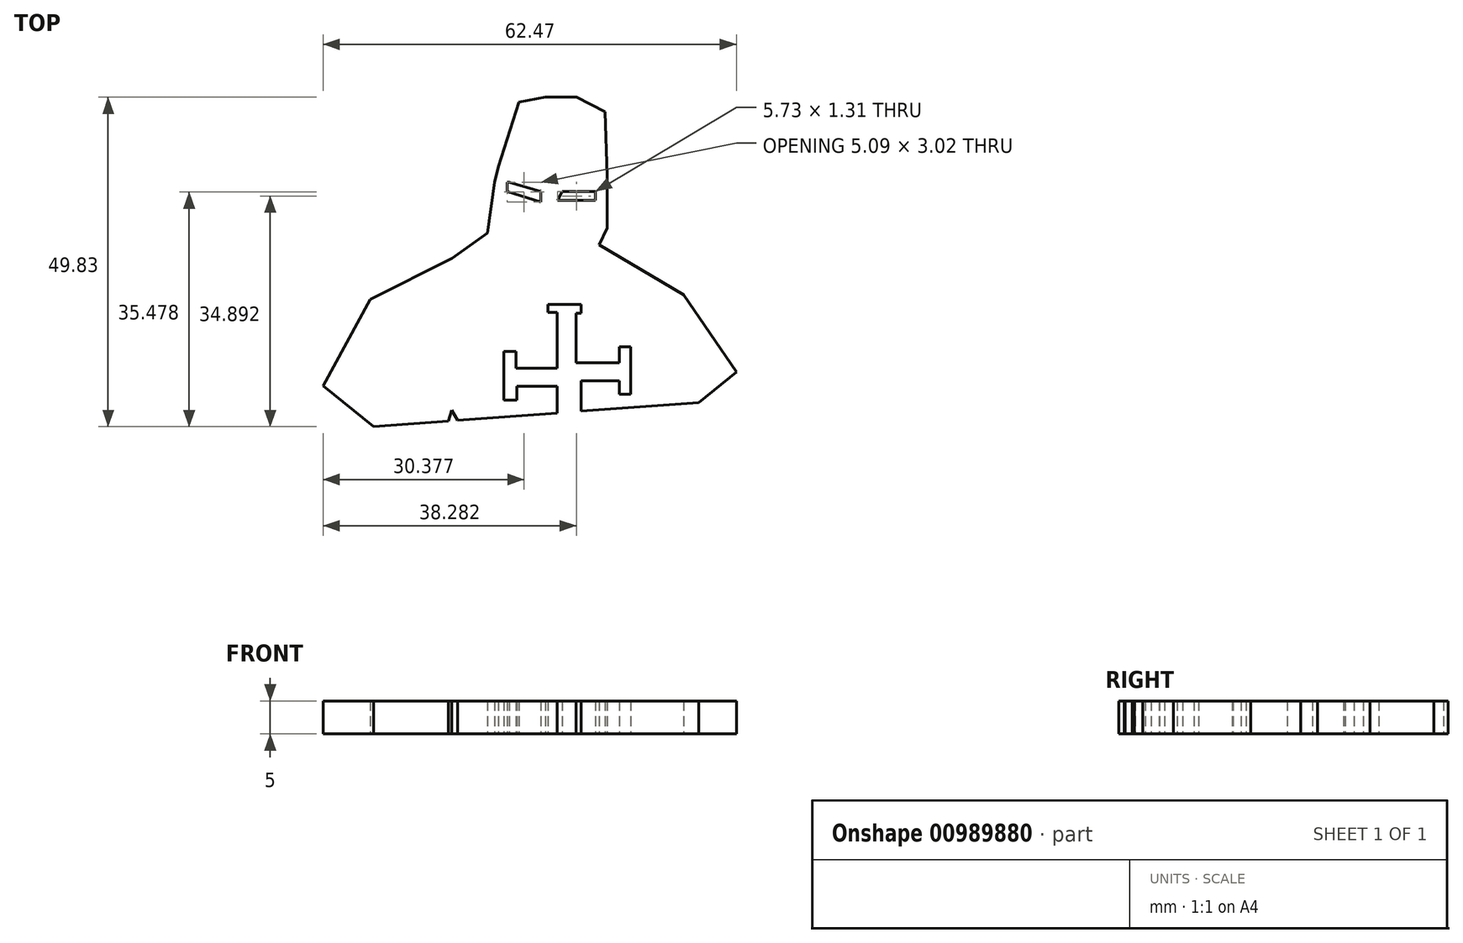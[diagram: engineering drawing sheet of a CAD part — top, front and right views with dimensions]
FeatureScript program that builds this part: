
annotation { "Feature Type Name" : "Feature", "Feature Type Description" : "" }
export const myFeature = defineFeature(function(context is Context, id is Id, definition is map)
    precondition{}
    {
        {
            var Q0;
            Q0=qCreatedBy(makeId("Top.planeOp"),FACE);
            var sketch = newSketch(context, id + "F0", { "sketchPlane" : qUnion([Q0])});
            skLineSegment(sketch, "E0", {"start": v(-38.63, 22.84) * mm, "end": v(-46.28, 28.98) * mm});
            skLineSegment(sketch, "E1", {"start": v(-46.28, 28.98) * mm, "end": v(-39.16, 42.1) * mm});
            skLineSegment(sketch, "E2", {"start": v(-39.16, 42.1) * mm, "end": v(-26.8, 48.3) * mm});
            skLineSegment(sketch, "E3", {"start": v(-26.8, 48.3) * mm, "end": v(-21.43, 52.1) * mm});
            skLineSegment(sketch, "E4", {"start": v(-21.43, 52.1) * mm, "end": v(-20.37, 59.83) * mm});
            skLineSegment(sketch, "E5", {"start": v(-20.37, 59.83) * mm, "end": v(-19.79, 62.17) * mm});
            skLineSegment(sketch, "E6", {"start": v(-19.79, 62.17) * mm, "end": v(-16.68, 71.92) * mm});
            skLineSegment(sketch, "E7", {"start": v(-16.68, 71.92) * mm, "end": v(-12.68, 72.67) * mm});
            skLineSegment(sketch, "E8", {"start": v(-12.68, 72.67) * mm, "end": v(-8, 72.67) * mm});
            skLineSegment(sketch, "E9", {"start": v(-8, 72.67) * mm, "end": v(-3.67, 70.46) * mm});
            skLineSegment(sketch, "E10", {"start": v(-3.67, 70.46) * mm, "end": v(-3.35, 60.81) * mm});
            skLineSegment(sketch, "E11", {"start": v(-3.35, 60.81) * mm, "end": v(-3.35, 52.88) * mm});
            skLineSegment(sketch, "E12", {"start": v(-3.35, 52.88) * mm, "end": v(-4.52, 50.32) * mm});
            skLineSegment(sketch, "E13", {"start": v(-4.52, 50.32) * mm, "end": v(8.23, 42.79) * mm});
            skLineSegment(sketch, "E14", {"start": v(8.23, 42.79) * mm, "end": v(16.19, 31.12) * mm});
            skLineSegment(sketch, "E15", {"start": v(16.19, 31.12) * mm, "end": v(10.5, 26.5) * mm});
            skLineSegment(sketch, "E16", {"start": v(10.5, 26.5) * mm, "end": v(-38.63, 22.84) * mm});
            skLineSegment(sketch, "E17", {"start": v(-18.15, 59.83) * mm, "end": v(-13.36, 58.39) * mm});
            skLineSegment(sketch, "E18", {"start": v(-13.36, 58.39) * mm, "end": v(-13.36, 56.8) * mm});
            skLineSegment(sketch, "E19", {"start": v(-13.36, 56.8) * mm, "end": v(-18.45, 58.39) * mm});
            skLineSegment(sketch, "E20", {"start": v(-18.45, 58.39) * mm, "end": v(-18.45, 59.83) * mm});
            skLineSegment(sketch, "E21", {"start": v(-18.45, 59.83) * mm, "end": v(-18.15, 59.83) * mm});
            skLineSegment(sketch, "E22", {"start": v(-10.87, 57.08) * mm, "end": v(-5.13, 57.08) * mm});
            skLineSegment(sketch, "E23", {"start": v(-5.13, 57.08) * mm, "end": v(-5.13, 58.39) * mm});
            skLineSegment(sketch, "E24", {"start": v(-5.13, 58.39) * mm, "end": v(-10.12, 58.39) * mm});
            skLineSegment(sketch, "E25", {"start": v(-10.12, 58.39) * mm, "end": v(-10.87, 57.08) * mm});
            skLineSegment(sketch, "E26", {"start": v(-7.27, 41.34) * mm, "end": v(-7.27, 40) * mm});
            skLineSegment(sketch, "E27", {"start": v(-7.27, 40) * mm, "end": v(-8.03, 40) * mm});
            skLineSegment(sketch, "E28", {"start": v(-8.03, 40) * mm, "end": v(-8.03, 32.47) * mm});
            skLineSegment(sketch, "E29", {"start": v(-8.03, 32.47) * mm, "end": v(-1.51, 32.47) * mm});
            skLineSegment(sketch, "E30", {"start": v(-1.51, 32.47) * mm, "end": v(-1.51, 34.91) * mm});
            skLineSegment(sketch, "E31", {"start": v(-1.51, 34.91) * mm, "end": v(0.2, 34.91) * mm});
            skLineSegment(sketch, "E32", {"start": v(0.2, 34.91) * mm, "end": v(0.2, 27.75) * mm});
            skLineSegment(sketch, "E33", {"start": v(0.2, 27.75) * mm, "end": v(-1.51, 27.75) * mm});
            skLineSegment(sketch, "E34", {"start": v(-1.51, 27.75) * mm, "end": v(-1.51, 29.78) * mm});
            skLineSegment(sketch, "E35", {"start": v(-1.51, 29.78) * mm, "end": v(-7.27, 29.78) * mm});
            skLineSegment(sketch, "E36", {"start": v(-7.27, 29.78) * mm, "end": v(-7.27, 25.18) * mm});
            skLineSegment(sketch, "E37", {"start": v(-7.27, 41.34) * mm, "end": v(-12.32, 41.34) * mm});
            skLineSegment(sketch, "E38", {"start": v(-12.32, 41.34) * mm, "end": v(-12.32, 40.15) * mm});
            skLineSegment(sketch, "E39", {"start": v(-12.32, 40.15) * mm, "end": v(-10.93, 40.15) * mm});
            skLineSegment(sketch, "E40", {"start": v(-10.93, 40.15) * mm, "end": v(-10.93, 31.67) * mm});
            skLineSegment(sketch, "E41", {"start": v(-10.93, 31.67) * mm, "end": v(-17.1, 31.67) * mm});
            skLineSegment(sketch, "E42", {"start": v(-17.1, 31.67) * mm, "end": v(-17.1, 34.2) * mm});
            skLineSegment(sketch, "E43", {"start": v(-17.1, 34.2) * mm, "end": v(-19, 34.2) * mm});
            skLineSegment(sketch, "E44", {"start": v(-19, 34.2) * mm, "end": v(-19, 26.85) * mm});
            skLineSegment(sketch, "E45", {"start": v(-19, 26.85) * mm, "end": v(-16.96, 26.85) * mm});
            skLineSegment(sketch, "E46", {"start": v(-16.96, 26.85) * mm, "end": v(-16.96, 28.93) * mm});
            skLineSegment(sketch, "E47", {"start": v(-16.96, 28.93) * mm, "end": v(-10.93, 28.93) * mm});
            skLineSegment(sketch, "E48", {"start": v(-10.93, 28.93) * mm, "end": v(-10.93, 24.9) * mm});
            skLineSegment(sketch, "E49", {"start": v(-27.33, 23.68) * mm, "end": v(-26.83, 25.35) * mm});
            skLineSegment(sketch, "E50", {"start": v(-26.83, 25.35) * mm, "end": v(-25.92, 23.79) * mm});
            skSolve(sketch);
        }
        {
            var Q0;
            {var subQ1=sQuery(id+"F0.wireOp",EDGE,"E0");Q0=makeQuery(id+"F0.imprint","IMPRINT",FACE,{"disambiguationData":[TD([[makeQuery(id+"F0.imprint","IMPRINT",EDGE,{"derivedFrom":subQ1}),-1.0]])]});}
            extrude(context, id + "F1", {"entities" : qUnion([Q0]), "depth" : 5 * mm, "offsetDistance" : 25 * mm});
        }
    });
